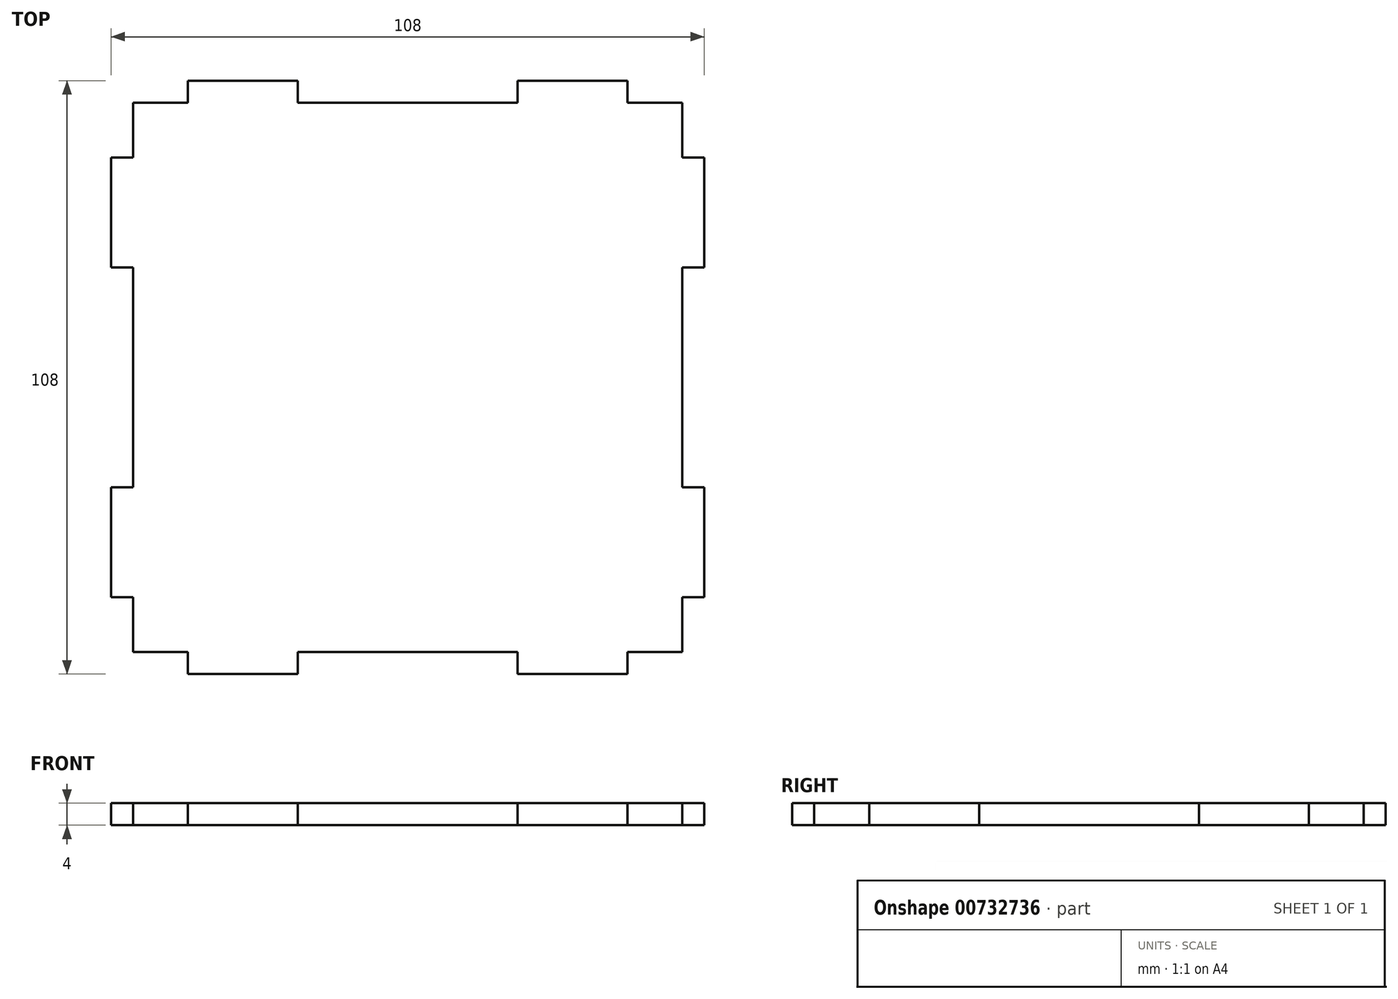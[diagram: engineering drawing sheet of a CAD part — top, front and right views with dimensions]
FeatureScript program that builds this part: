
annotation { "Feature Type Name" : "Feature", "Feature Type Description" : "" }
export const myFeature = defineFeature(function(context is Context, id is Id, definition is map)
    precondition{}
    {
        {
            var Q0;
            Q0=qCreatedBy(makeId("Top.planeOp"),FACE);
            var sketch = newSketch(context, id + "F0", { "sketchPlane" : qUnion([Q0])});
            skLineSegment(sketch, "E0.bottom", {"start": v(50, 50) * mm, "end": v(40, 50) * mm});
            skLineSegment(sketch, "E0.top", {"start": v(50, -50) * mm, "end": v(40, -50) * mm});
            skLineSegment(sketch, "E0.left", {"start": v(50, 50) * mm, "end": v(50, 40) * mm});
            skLineSegment(sketch, "E0.right", {"start": v(-50, 50) * mm, "end": v(-50, 40) * mm});
            skPoint(sketch, "E0.middle", {"position": v(0, 0) * mm});
            skLineSegment(sketch, "E1.bottom", {"start": v(-50, 40) * mm, "end": v(-54, 40) * mm});
            skLineSegment(sketch, "E1.top", {"start": v(-50, 20) * mm, "end": v(-54, 20) * mm});
            skLineSegment(sketch, "E1.right", {"start": v(-54, 40) * mm, "end": v(-54, 20) * mm});
            skLineSegment(sketch, "E2.MirrorCS", {"start": v(50, 40) * mm, "end": v(54, 40) * mm});
            skLineSegment(sketch, "E3.MirrorCS", {"start": v(50, 20) * mm, "end": v(54, 20) * mm});
            skLineSegment(sketch, "E4.MirrorCS", {"start": v(54, 40) * mm, "end": v(54, 20) * mm});
            skLineSegment(sketch, "E5.MirrorCS", {"start": v(50, -40) * mm, "end": v(54, -40) * mm});
            skLineSegment(sketch, "E6.MirrorCS", {"start": v(50, -20) * mm, "end": v(54, -20) * mm});
            skLineSegment(sketch, "E7.MirrorCS", {"start": v(-50, -20) * mm, "end": v(-54, -20) * mm});
            skLineSegment(sketch, "E8.MirrorCS", {"start": v(-50, -40) * mm, "end": v(-54, -40) * mm});
            skLineSegment(sketch, "E9.MirrorCS", {"start": v(54, -40) * mm, "end": v(54, -20) * mm});
            skLineSegment(sketch, "E10.MirrorCS", {"start": v(-54, -40) * mm, "end": v(-54, -20) * mm});
            skLineSegment(sketch, "E11.trimOffspring", {"start": v(-50, 20) * mm, "end": v(-50, -20) * mm});
            skLineSegment(sketch, "E12.trimOffspring", {"start": v(50, 20) * mm, "end": v(50, -20) * mm});
            skLineSegment(sketch, "E13.trimOffspring", {"start": v(50, -40) * mm, "end": v(50, -50) * mm});
            skLineSegment(sketch, "E14.trimOffspring", {"start": v(-50, -40) * mm, "end": v(-50, -50) * mm});
            skLineSegment(sketch, "E15.top", {"start": v(-40, 54) * mm, "end": v(-20, 54) * mm});
            skLineSegment(sketch, "E15.left", {"start": v(-40, 50) * mm, "end": v(-40, 54) * mm});
            skLineSegment(sketch, "E15.right", {"start": v(-20, 50) * mm, "end": v(-20, 54) * mm});
            skLineSegment(sketch, "E16.trimOffspring", {"start": v(-40, 50) * mm, "end": v(-50, 50) * mm});
            skLineSegment(sketch, "E17.MirrorCS", {"start": v(40, 54) * mm, "end": v(20, 54) * mm});
            skLineSegment(sketch, "E18.MirrorCS", {"start": v(40, 50) * mm, "end": v(40, 54) * mm});
            skLineSegment(sketch, "E19.MirrorCS", {"start": v(20, 50) * mm, "end": v(20, 54) * mm});
            skLineSegment(sketch, "E20.trimOffspring", {"start": v(20, 50) * mm, "end": v(-20, 50) * mm});
            skLineSegment(sketch, "E21.MirrorCS", {"start": v(40, -54) * mm, "end": v(20, -54) * mm});
            skLineSegment(sketch, "E22.MirrorCS", {"start": v(40, -50) * mm, "end": v(40, -54) * mm});
            skLineSegment(sketch, "E23.MirrorCS", {"start": v(20, -50) * mm, "end": v(20, -54) * mm});
            skLineSegment(sketch, "E24.MirrorCS", {"start": v(-20, -50) * mm, "end": v(-20, -54) * mm});
            skLineSegment(sketch, "E25.MirrorCS", {"start": v(-40, -54) * mm, "end": v(-20, -54) * mm});
            skLineSegment(sketch, "E26.MirrorCS", {"start": v(-40, -50) * mm, "end": v(-40, -54) * mm});
            skLineSegment(sketch, "E27.trimOffspring", {"start": v(-40, -50) * mm, "end": v(-50, -50) * mm});
            skLineSegment(sketch, "E28.trimOffspring", {"start": v(20, -50) * mm, "end": v(-20, -50) * mm});
            skSolve(sketch);
        }
        {
            var Q0;
            Q0=makeQuery(id+"F0.imprint","IMPRINT",FACE,{"disambiguationData":[TD([[makeQuery(id+"F0.imprint","IMPRINT",EDGE,{"derivedFrom":sQuery(id+"F0.wireOp",EDGE,"tXzo0Muj-3qYD-Yrpu-env9-NPLb1Lz4Y9nM.bottom")}),1.0]])]});
            var Q1;
            Q1=makeQuery(id+"F0.imprint","IMPRINT",FACE,{"disambiguationData":[TD([[makeQuery(id+"F0.imprint","IMPRINT",EDGE,{"derivedFrom":sQuery(id+"F0.wireOp",EDGE,"E0.bottom")}),1.0]])]});
            extrude(context, id + "F1", {"entities" : qUnion([Q0, Q1]), "depth" : 4 * mm, "offsetDistance" : 25 * mm});
        }
    });
